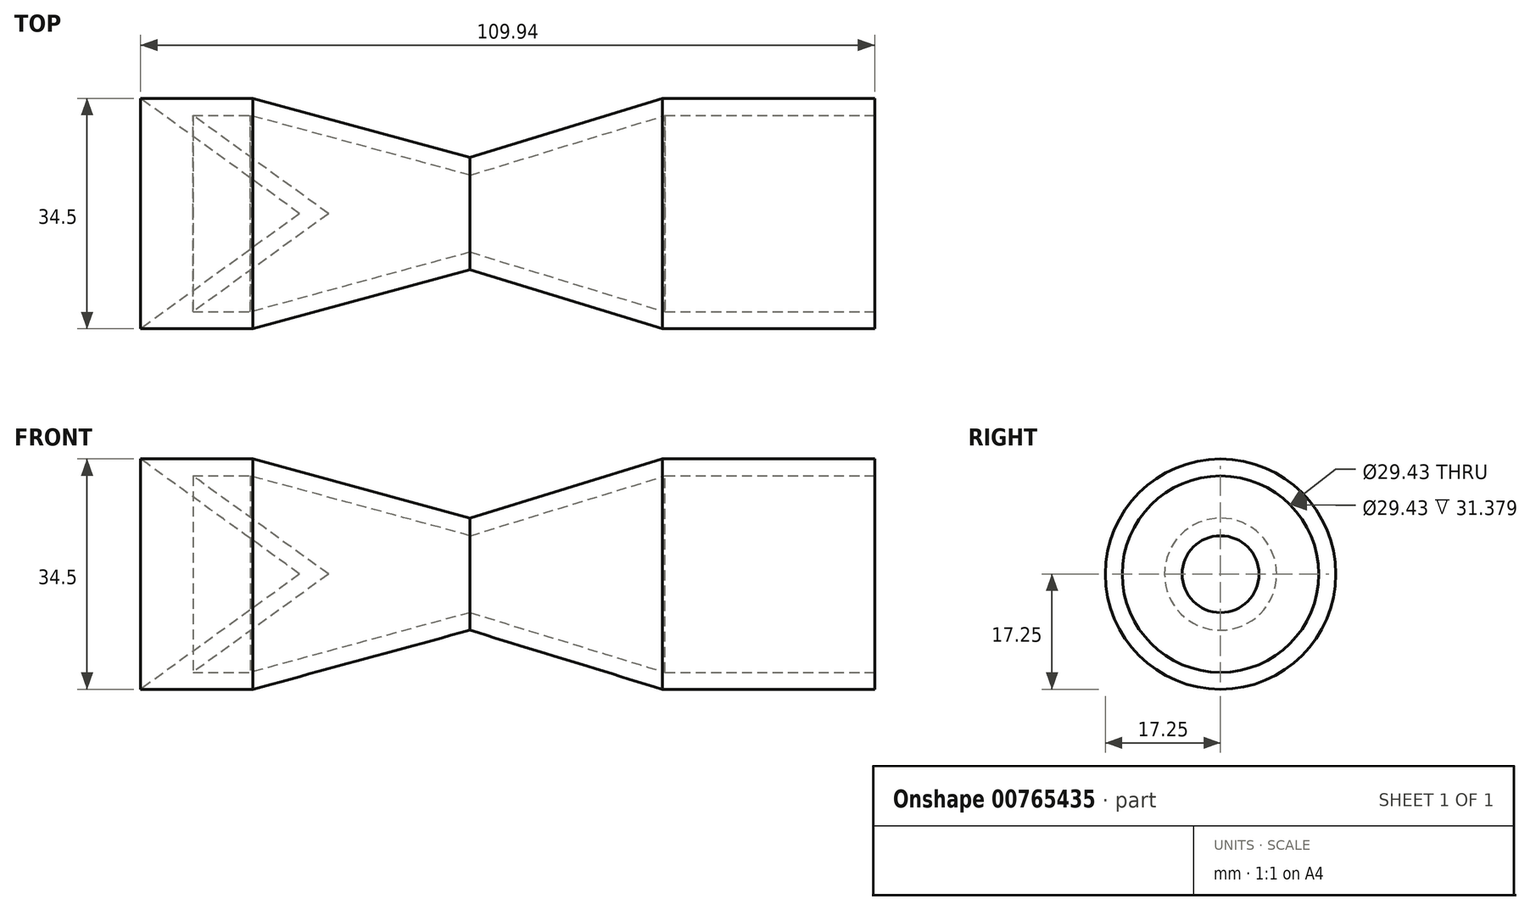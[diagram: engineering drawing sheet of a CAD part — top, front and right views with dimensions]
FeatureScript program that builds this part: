
annotation { "Feature Type Name" : "Feature", "Feature Type Description" : "" }
export const myFeature = defineFeature(function(context is Context, id is Id, definition is map)
    precondition{}
    {
        {
            var Q0;
            Q0=qCreatedBy(makeId("Front.planeOp"),FACE);
            var sketch = newSketch(context, id + "F0", { "sketchPlane" : qUnion([Q0])});
            skPoint(sketch, "E0.end.orphan", {"position": v(40, 0) * mm});
            skPoint(sketch, "E1.orphan", {"position": v(0, 0) * mm});
            skPoint(sketch, "E2.end.orphan", {"position": v(80.01, 0) * mm});
            skPoint(sketch, "E3.center.orphan", {"position": v(60, 0) * mm});
            skLineSegment(sketch, "E4.MirrorCS", {"start": v(-32.52, 17.25) * mm, "end": v(-49.32, 17.25) * mm});
            skLineSegment(sketch, "E5", {"start": v(-32.52, 17.25) * mm, "end": v(0, 8.4) * mm});
            skLineSegment(sketch, "E6", {"start": v(0, 8.4) * mm, "end": v(28.86, 17.25) * mm});
            skLineSegment(sketch, "E7", {"start": v(28.86, 17.25) * mm, "end": v(60.62, 17.25) * mm});
            skPoint(sketch, "E8.end.orphan", {"position": v(-32.52, -17.25) * mm});
            skPoint(sketch, "E9.start.orphan", {"position": v(-49.32, -17.25) * mm});
            skPoint(sketch, "E10.MirrorCS.end.orphan", {"position": v(-32.52, 17.25) * mm});
            skPoint(sketch, "E10.MirrorCS.start.orphan", {"position": v(-25.5, 0) * mm});
            skPoint(sketch, "E11.end.orphan", {"position": v(-49.32, 0) * mm});
            skLineSegment(sketch, "E12", {"start": v(-49.32, 17.25) * mm, "end": v(-25.5, 0) * mm});
            skLineSegment(sketch, "E13", {"start": v(60.62, 17.25) * mm, "end": v(60.62, 0) * mm});
            skLineSegment(sketch, "E14", {"start": v(60.62, 0) * mm, "end": v(-25.5, 0) * mm});
            skSolve(sketch);
        }
        {
            var Q0;
            Q0=makeQuery(id+"F0.imprint","IMPRINT",FACE,{"disambiguationData":[TD([[makeQuery(id+"F0.imprint","IMPRINT",EDGE,{"derivedFrom":sQuery(id+"F0.wireOp",EDGE,"E4.MirrorCS")}),1.0]])]});
            var Q1;
            Q1=sQuery(id+"F0.wireOp",EDGE,"E14");
            revolve(context, id + "F1", {"surfaceOperationType" : NewSurfaceOperationType.NEW, "entities" : qUnion([Q0]), "axis" : qUnion([Q1]), "revolveType" : RevolveType.FULL});
        }
        {
            var Q0;
            Q0=makeQuery(id+"F1.opRevolve","SWEPT_FACE",FACE,{"disambiguationData":[OSD([sQuery(id+"F0.wireOp",EDGE,"E13")])]});
            shell(context, id + "F2", {"entities" : qUnion([Q0]), "thickness" : 2.54 * mm});
        }
    });
